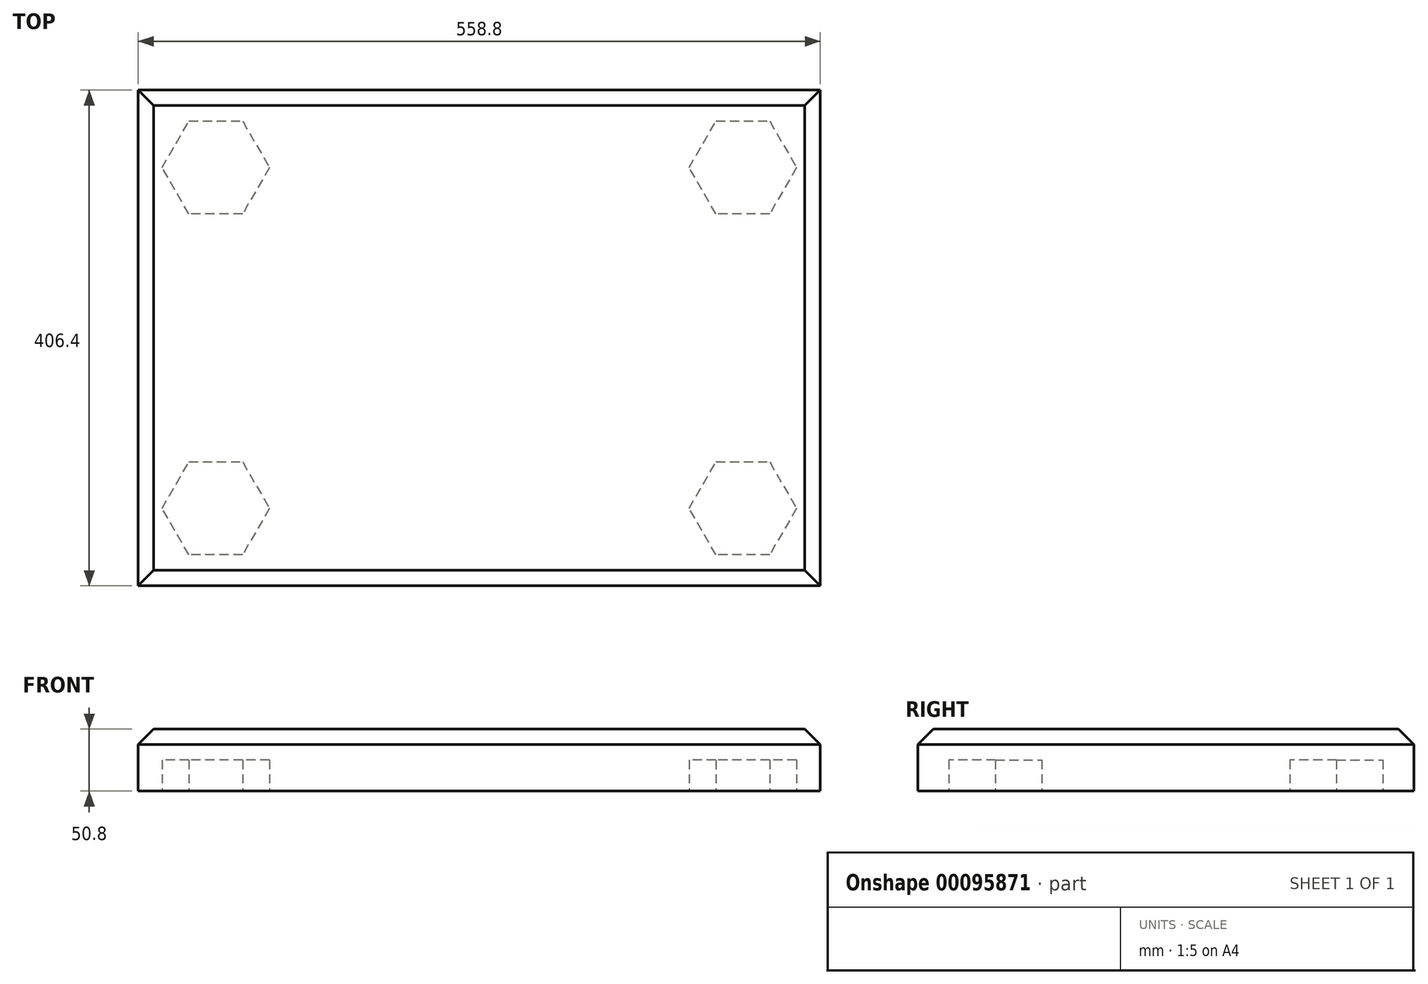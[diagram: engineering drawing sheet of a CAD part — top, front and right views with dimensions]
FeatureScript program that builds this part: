
annotation { "Feature Type Name" : "Feature", "Feature Type Description" : "" }
export const myFeature = defineFeature(function(context is Context, id is Id, definition is map)
    precondition{}
    {
        {
            var Q0;
            Q0=qCreatedBy(makeId("Top.planeOp"),FACE);
            var sketch = newSketch(context, id + "F0", { "sketchPlane" : qUnion([Q0])});
            skLineSegment(sketch, "E0.bottom", {"start": v(279.4, 203.2) * mm, "end": v(-279.4, 203.2) * mm});
            skLineSegment(sketch, "E0.top", {"start": v(279.4, -203.2) * mm, "end": v(-279.4, -203.2) * mm});
            skLineSegment(sketch, "E0.left", {"start": v(279.4, 203.2) * mm, "end": v(279.4, -203.2) * mm});
            skLineSegment(sketch, "E0.right", {"start": v(-279.4, 203.2) * mm, "end": v(-279.4, -203.2) * mm});
            skPoint(sketch, "E0.middle", {"position": v(0, 0) * mm});
            skCircle(sketch, "E1.cCircle", {"center": v(-215.9, -139.7) * mm, "radius": 38.1 * mm, "construction": true});
            skLineSegment(sketch, "E1.0", {"start": v(-193.9, -177.8) * mm, "end": v(-237.9, -177.8) * mm});
            skLineSegment(sketch, "E1.1", {"start": v(-237.9, -177.8) * mm, "end": v(-259.9, -139.7) * mm});
            skLineSegment(sketch, "E1.2", {"start": v(-259.9, -139.7) * mm, "end": v(-237.9, -101.6) * mm});
            skLineSegment(sketch, "E1.3", {"start": v(-237.9, -101.6) * mm, "end": v(-193.9, -101.6) * mm});
            skLineSegment(sketch, "E1.4", {"start": v(-193.9, -101.6) * mm, "end": v(-171.9, -139.7) * mm});
            skLineSegment(sketch, "E1.5", {"start": v(-171.9, -139.7) * mm, "end": v(-193.9, -177.8) * mm});
            skPoint(sketch, "E1.0.midPoint", {"position": v(-215.9, -177.8) * mm});
            skCircle(sketch, "E2.cCircle", {"center": v(215.9, -139.7) * mm, "radius": 38.1 * mm, "construction": true});
            skLineSegment(sketch, "E2.0", {"start": v(237.9, -177.8) * mm, "end": v(193.9, -177.8) * mm});
            skLineSegment(sketch, "E2.1", {"start": v(193.9, -177.8) * mm, "end": v(171.9, -139.7) * mm});
            skLineSegment(sketch, "E2.2", {"start": v(171.9, -139.7) * mm, "end": v(193.9, -101.6) * mm});
            skLineSegment(sketch, "E2.3", {"start": v(193.9, -101.6) * mm, "end": v(237.9, -101.6) * mm});
            skLineSegment(sketch, "E2.4", {"start": v(237.9, -101.6) * mm, "end": v(259.9, -139.7) * mm});
            skLineSegment(sketch, "E2.5", {"start": v(259.9, -139.7) * mm, "end": v(237.9, -177.8) * mm});
            skPoint(sketch, "E2.0.midPoint", {"position": v(215.9, -177.8) * mm});
            skCircle(sketch, "E3.cCircle", {"center": v(-215.9, 139.7) * mm, "radius": 38.1 * mm, "construction": true});
            skLineSegment(sketch, "E3.0", {"start": v(-193.9, 101.6) * mm, "end": v(-237.9, 101.6) * mm});
            skLineSegment(sketch, "E3.1", {"start": v(-237.9, 101.6) * mm, "end": v(-259.9, 139.7) * mm});
            skLineSegment(sketch, "E3.2", {"start": v(-259.9, 139.7) * mm, "end": v(-237.9, 177.8) * mm});
            skLineSegment(sketch, "E3.3", {"start": v(-237.9, 177.8) * mm, "end": v(-193.9, 177.8) * mm});
            skLineSegment(sketch, "E3.4", {"start": v(-193.9, 177.8) * mm, "end": v(-171.9, 139.7) * mm});
            skLineSegment(sketch, "E3.5", {"start": v(-171.9, 139.7) * mm, "end": v(-193.9, 101.6) * mm});
            skPoint(sketch, "E3.0.midPoint", {"position": v(-215.9, 101.6) * mm});
            skCircle(sketch, "E4.cCircle", {"center": v(215.9, 139.7) * mm, "radius": 38.1 * mm, "construction": true});
            skLineSegment(sketch, "E4.0", {"start": v(237.9, 101.6) * mm, "end": v(193.9, 101.6) * mm});
            skLineSegment(sketch, "E4.1", {"start": v(193.9, 101.6) * mm, "end": v(171.9, 139.7) * mm});
            skLineSegment(sketch, "E4.2", {"start": v(171.9, 139.7) * mm, "end": v(193.9, 177.8) * mm});
            skLineSegment(sketch, "E4.3", {"start": v(193.9, 177.8) * mm, "end": v(237.9, 177.8) * mm});
            skLineSegment(sketch, "E4.4", {"start": v(237.9, 177.8) * mm, "end": v(259.9, 139.7) * mm});
            skLineSegment(sketch, "E4.5", {"start": v(259.9, 139.7) * mm, "end": v(237.9, 101.6) * mm});
            skPoint(sketch, "E4.0.midPoint", {"position": v(215.9, 101.6) * mm});
            skSolve(sketch);
        }
        {
            var Q0;
            Q0=makeQuery(id+"F0.imprint","IMPRINT",FACE,{"disambiguationData":[TD([[makeQuery(id+"F0.imprint","IMPRINT",EDGE,{"derivedFrom":sQuery(id+"F0.wireOp",EDGE,"E0.bottom")}),1.0]])]});
            extrude(context, id + "F1", {"entities" : qUnion([Q0]), "depth" : 50.8 * mm});
        }
        {
            var Q0;
            Q0=makeQuery(id+"F1.opExtrude","CAP_FACE",FACE,{"disambiguationData":[OSD([sQuery(id+"F0.wireOp",EDGE,"E0.bottom"),sQuery(id+"F0.wireOp",EDGE,"E0.top"),sQuery(id+"F0.wireOp",EDGE,"E0.left"),sQuery(id+"F0.wireOp",EDGE,"E0.right"),sQuery(id+"F0.wireOp",EDGE,"E1.0"),sQuery(id+"F0.wireOp",EDGE,"E1.1"),sQuery(id+"F0.wireOp",EDGE,"E1.2"),sQuery(id+"F0.wireOp",EDGE,"E1.3"),sQuery(id+"F0.wireOp",EDGE,"E1.4"),sQuery(id+"F0.wireOp",EDGE,"E1.5"),sQuery(id+"F0.wireOp",EDGE,"E2.0"),sQuery(id+"F0.wireOp",EDGE,"E2.1"),sQuery(id+"F0.wireOp",EDGE,"E2.2"),sQuery(id+"F0.wireOp",EDGE,"E2.3"),sQuery(id+"F0.wireOp",EDGE,"E2.4"),sQuery(id+"F0.wireOp",EDGE,"E2.5"),sQuery(id+"F0.wireOp",EDGE,"E3.0"),sQuery(id+"F0.wireOp",EDGE,"E3.1"),sQuery(id+"F0.wireOp",EDGE,"E3.2"),sQuery(id+"F0.wireOp",EDGE,"E3.3"),sQuery(id+"F0.wireOp",EDGE,"E3.4"),sQuery(id+"F0.wireOp",EDGE,"E3.5"),sQuery(id+"F0.wireOp",EDGE,"E4.0"),sQuery(id+"F0.wireOp",EDGE,"E4.1"),sQuery(id+"F0.wireOp",EDGE,"E4.2"),sQuery(id+"F0.wireOp",EDGE,"E4.3"),sQuery(id+"F0.wireOp",EDGE,"E4.4"),sQuery(id+"F0.wireOp",EDGE,"E4.5")])],"isStart":false});
            var sketch = newSketch(context, id + "F2", { "sketchPlane" : qUnion([Q0])});
            skPoint(sketch, "E5.middle", {"position": v(-141.74, 104.72) * mm});
            skCircle(sketch, "E6.cCircle", {"center": v(-215.9, -139.7) * mm, "radius": 38.1 * mm, "construction": true});
            skLineSegment(sketch, "E6.0", {"start": v(-193.9, -177.8) * mm, "end": v(-237.9, -177.8) * mm});
            skLineSegment(sketch, "E6.1", {"start": v(-237.9, -177.8) * mm, "end": v(-259.9, -139.7) * mm});
            skLineSegment(sketch, "E6.2", {"start": v(-259.9, -139.7) * mm, "end": v(-237.9, -101.6) * mm});
            skLineSegment(sketch, "E6.3", {"start": v(-237.9, -101.6) * mm, "end": v(-193.9, -101.6) * mm});
            skLineSegment(sketch, "E6.4", {"start": v(-193.9, -101.6) * mm, "end": v(-171.9, -139.7) * mm});
            skLineSegment(sketch, "E6.5", {"start": v(-171.9, -139.7) * mm, "end": v(-193.9, -177.8) * mm});
            skPoint(sketch, "E6.0.midPoint", {"position": v(-215.9, -177.8) * mm});
            skCircle(sketch, "E7.cCircle", {"center": v(215.9, -139.7) * mm, "radius": 38.1 * mm, "construction": true});
            skLineSegment(sketch, "E7.0", {"start": v(237.9, -177.8) * mm, "end": v(193.9, -177.8) * mm});
            skLineSegment(sketch, "E7.1", {"start": v(193.9, -177.8) * mm, "end": v(171.9, -139.7) * mm});
            skLineSegment(sketch, "E7.2", {"start": v(171.9, -139.7) * mm, "end": v(193.9, -101.6) * mm});
            skLineSegment(sketch, "E7.3", {"start": v(193.9, -101.6) * mm, "end": v(237.9, -101.6) * mm});
            skLineSegment(sketch, "E7.4", {"start": v(237.9, -101.6) * mm, "end": v(259.9, -139.7) * mm});
            skLineSegment(sketch, "E7.5", {"start": v(259.9, -139.7) * mm, "end": v(237.9, -177.8) * mm});
            skPoint(sketch, "E7.0.midPoint", {"position": v(215.9, -177.8) * mm});
            skCircle(sketch, "E8.cCircle", {"center": v(-215.9, 139.7) * mm, "radius": 38.1 * mm, "construction": true});
            skLineSegment(sketch, "E8.0", {"start": v(-193.9, 101.6) * mm, "end": v(-237.9, 101.6) * mm});
            skLineSegment(sketch, "E8.1", {"start": v(-237.9, 101.6) * mm, "end": v(-259.9, 139.7) * mm});
            skLineSegment(sketch, "E8.2", {"start": v(-259.9, 139.7) * mm, "end": v(-237.9, 177.8) * mm});
            skLineSegment(sketch, "E8.3", {"start": v(-237.9, 177.8) * mm, "end": v(-193.9, 177.8) * mm});
            skLineSegment(sketch, "E8.4", {"start": v(-193.9, 177.8) * mm, "end": v(-171.9, 139.7) * mm});
            skLineSegment(sketch, "E8.5", {"start": v(-171.9, 139.7) * mm, "end": v(-193.9, 101.6) * mm});
            skPoint(sketch, "E8.0.midPoint", {"position": v(-215.9, 101.6) * mm});
            skCircle(sketch, "E9.cCircle", {"center": v(215.9, 139.7) * mm, "radius": 38.1 * mm, "construction": true});
            skLineSegment(sketch, "E9.0", {"start": v(237.9, 101.6) * mm, "end": v(193.9, 101.6) * mm});
            skLineSegment(sketch, "E9.1", {"start": v(193.9, 101.6) * mm, "end": v(171.9, 139.7) * mm});
            skLineSegment(sketch, "E9.2", {"start": v(171.9, 139.7) * mm, "end": v(193.9, 177.8) * mm});
            skLineSegment(sketch, "E9.3", {"start": v(193.9, 177.8) * mm, "end": v(237.9, 177.8) * mm});
            skLineSegment(sketch, "E9.4", {"start": v(237.9, 177.8) * mm, "end": v(259.9, 139.7) * mm});
            skLineSegment(sketch, "E9.5", {"start": v(259.9, 139.7) * mm, "end": v(237.9, 101.6) * mm});
            skPoint(sketch, "E9.0.midPoint", {"position": v(215.9, 101.6) * mm});
            skSolve(sketch);
        }
        {
            var Q0;
            Q0=makeQuery(id+"F2.imprint","IMPRINT",FACE,{"disambiguationData":[TD([[makeQuery(id+"F2.imprint","IMPRINT",EDGE,{"derivedFrom":sQuery(id+"F2.wireOp",EDGE,"E8.0")}),-1.0]])]});
            var Q1;
            Q1=makeQuery(id+"F2.imprint","IMPRINT",FACE,{"disambiguationData":[TD([[makeQuery(id+"F2.imprint","IMPRINT",EDGE,{"derivedFrom":sQuery(id+"F2.wireOp",EDGE,"E9.0")}),-1.0]])]});
            var Q2;
            Q2=makeQuery(id+"F2.imprint","IMPRINT",FACE,{"disambiguationData":[TD([[makeQuery(id+"F2.imprint","IMPRINT",EDGE,{"derivedFrom":sQuery(id+"F2.wireOp",EDGE,"E6.0")}),-1.0]])]});
            var Q3;
            Q3=makeQuery(id+"F2.imprint","IMPRINT",FACE,{"disambiguationData":[TD([[makeQuery(id+"F2.imprint","IMPRINT",EDGE,{"derivedFrom":sQuery(id+"F2.wireOp",EDGE,"E7.0")}),-1.0]])]});
            extrude(context, id + "F3", {"entities" : qUnion([Q0, Q1, Q2, Q3]), "operationType" : NewBodyOperationType.ADD, "oppositeDirection" : true, "depth" : 25.4 * mm});
        }
        {
            var Q0;
            Q0=makeQuery(id+"F1.opExtrude","CAP_EDGE",EDGE,{"disambiguationData":[OSD([sQuery(id+"F0.wireOp",EDGE,"E0.left")])],"isStart":false});
            var Q1;
            Q1=makeQuery(id+"F1.opExtrude","CAP_EDGE",EDGE,{"disambiguationData":[OSD([sQuery(id+"F0.wireOp",EDGE,"E0.top")])],"isStart":false});
            var Q2;
            Q2=makeQuery(id+"F1.opExtrude","CAP_EDGE",EDGE,{"disambiguationData":[OSD([sQuery(id+"F0.wireOp",EDGE,"E0.bottom")])],"isStart":false});
            var Q3;
            Q3=makeQuery(id+"F1.opExtrude","CAP_EDGE",EDGE,{"disambiguationData":[OSD([sQuery(id+"F0.wireOp",EDGE,"E0.right")])],"isStart":false});
            chamfer(context, id + "F4", {"entities" : qUnion([Q0, Q1, Q2, Q3]), "width" : 12.7 * mm, "tangentPropagation" : true});
        }
    });
